# Revit family: HL_Дворовый трап серии Perfekt_HL615HSW
name_source: partatom
category: Instalační zařizovací předměty
revit_build: Autodesk Revit 2016 (Build: 20161004_0715(x64)
units: mm (PartAtom-declared; Revit-internal decimal feet)

## family parameters
Bod výpočtu místnosti = Ano
Kóta kulaté spojky = Použít průměr
Nadpis OmniClass = Deck Waste Water Drains
Ořezat dutým tvarem při načtení = Ne
Sdílené = Ne
Typ součásti = Normální
Vždy vertikální = Ano
Založené na pracovní rovině = Ne
Číslo OmniClass = 23.70.50.21.24.14

## types (1)
- HL_Дворовый трап серии Perfekt_HL615HSW
    EAN = 9003076011490
    Klíčová poznámka = HL615HSW
    Komentáře k typům = Дворовый трап серии Perfekt DN110 горизонтальный с битумным полотном, 240х240мм ПП/226х226мм нержавеющая сталь с водяным затвором.
    Model = HL615HSW
    Popis = Дворовый трап серии Perfekt DN110 горизонтальный выпуск
    Připojení CW = Ne
    Připojení HW = Ne
    Připojení odpadu = Ano
    Připojení ventilace = Ne
    URL = http://www.hutterer-lechner.com
    Výrobce = HL Hutterer & Lechner GmbH
    ВЕС = 4,5 kg
    ВЫСОТА МОНТАЖА = 218 mm
    МАКСИМАЛЬНАЯ НАГРУЗКА КЛАССА = L - 1,5 t
    МАТЕРИАЛ = PP
    НАСАДКА = 42-130mm/240x240mm
    НОМИНАЛЬНЫЙ ДИАМЕТР = 110 mm
    ПРОИЗВОДИТЕЛЬНОСТЬ = 2,5 l/s
    РАЗМЕР = DN110
    РЕШЁТКА = Edelstahl 226x226mm

## geometry (parser evidence)
native form markers: Sweep x2
no freeform markers — native parametric forms only
